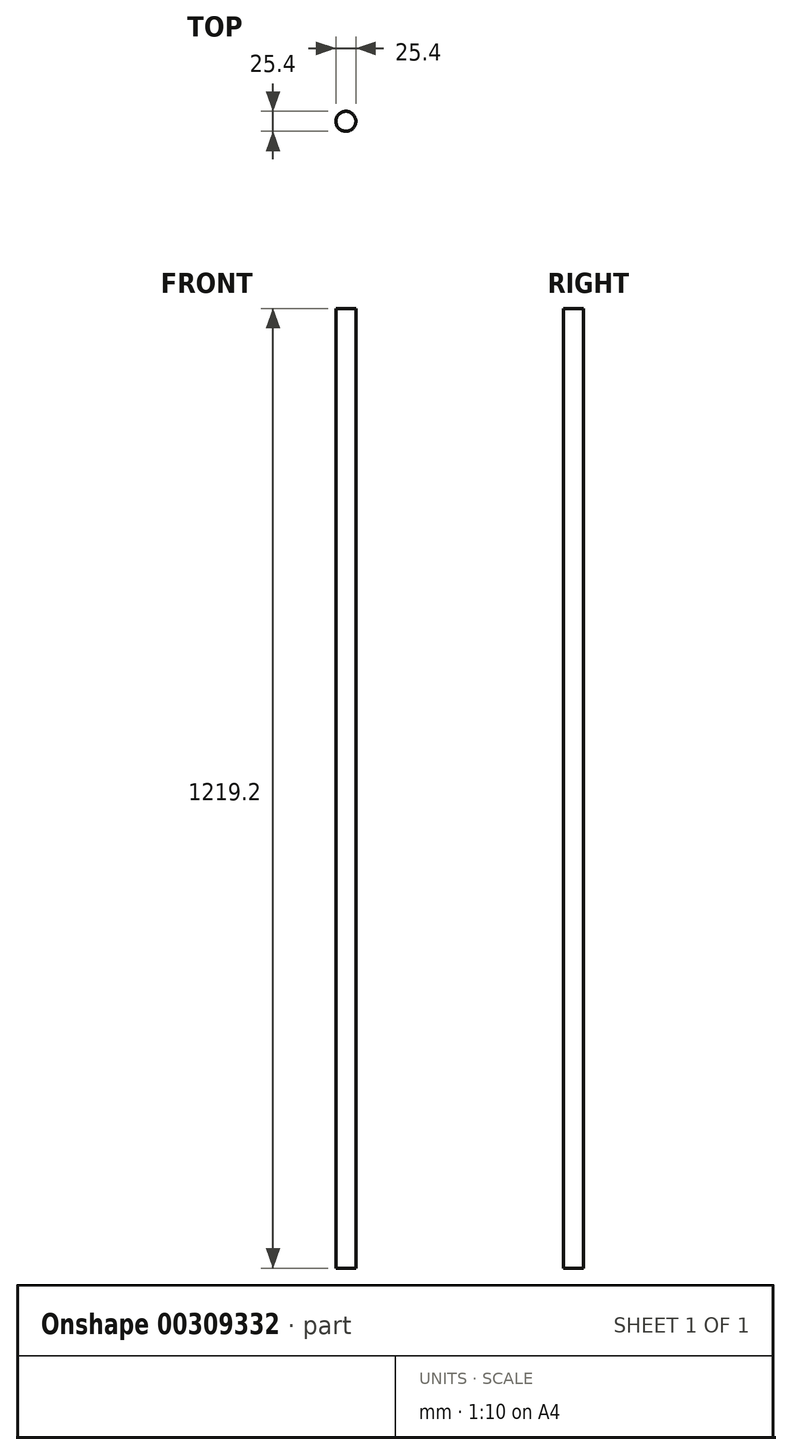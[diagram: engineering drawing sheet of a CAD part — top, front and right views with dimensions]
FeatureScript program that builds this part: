
annotation { "Feature Type Name" : "Feature", "Feature Type Description" : "" }
export const myFeature = defineFeature(function(context is Context, id is Id, definition is map)
    precondition{}
    {
        {
            var Q0;
            Q0=qCreatedBy(makeId("Front.planeOp"),FACE);
            var sketch = newSketch(context, id + "F0", { "sketchPlane" : qUnion([Q0])});
            skLineSegment(sketch, "E0", {"start": v(-28.18, -102.58) * mm, "end": v(-28.18, 1116.62) * mm});
            skLineSegment(sketch, "E1", {"start": v(-28.18, 1116.62) * mm, "end": v(-15.48, 1116.62) * mm});
            skLineSegment(sketch, "E2", {"start": v(-15.48, 1116.62) * mm, "end": v(-15.48, -102.58) * mm});
            skLineSegment(sketch, "E3", {"start": v(-28.18, -102.58) * mm, "end": v(-15.48, -102.58) * mm});
            skSolve(sketch);
        }
        {
            var Q0;
            Q0 = qSketchRegion(id + "F0", true);
            var Q1;
            Q1=sQuery(id+"F0.wireOp",EDGE,"E0");
            revolve(context, id + "F1", {"entities" : qUnion([Q0]), "axis" : qUnion([Q1]), "revolveType" : RevolveType.FULL});
        }
    });
